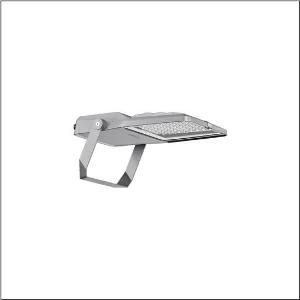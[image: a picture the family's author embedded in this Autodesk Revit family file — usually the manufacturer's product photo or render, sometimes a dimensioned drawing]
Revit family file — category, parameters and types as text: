
# Revit family: floodlight_fl_21_iq_mini___pl64_5xa7772b5e1a_cdb2
name_source: partatom
category: Lighting Fixtures
units: mm (PartAtom-declared; Revit-internal decimal feet)

## family parameters
Cut with Voids When Loaded = No
Host = Face
Light Source = No
Part Type = Normal
Room Calculation Point = No
Round Connector Dimension = Use Diameter
Shared = No

## types (1)
- --- (1 x LED, 5620 lm, 45.5 W, 4000K)
    Apparent Load = 46 VA
    CIE Flux Codes = 28 80 98 100 100
    Color Rendering = 80
    Color Temperature = 4000K
    Default Elevation = 1800 mm
    Description = Floodlight FL 21 iQ mini, floodlight, primary light control with lens, of PMMA, primary optical cover: protective disc, of toughened safety glass, transparent, light distribution: PL64, light emission: direct distribution, installation type: surface-mounted, LED, High Power LED, rated luminous flux: 5.620lm, luminous efficacy: 124lm/W, light colour: 840, colour temperature: 4000K, control: Street-Remote, Auto-Match, Temp-Guard, Night-Set, Smart-Wire, Desk-Remote (wireless, voltage-free reading and setting of iQ features in the workshop via application-optimized NFC function/RFID function), optimised constant luminous flux control (CLO 2.0), with terminal, 6-pole, mains connection: 220..240V, AC, 50/60Hz, start of lifetime: 46W, end of service life: 48W, reduction: 22W, luminaire housing, of diecast aluminium, powder-coated, Siteco® metallic grey (DB 702S), corrosivity category C5 mid according to DIN EN ISO 12944, sealing non-destructively replaceable, mounting bracket, of steel, galvanised, powder-coated, Siteco® metallic grey (DB 702S), protection rating (complete): IP66, insulation class (complete): insulation class II (safety insulation), certification: CE, ENEC, VDE, protection symbol: D, impact resistance: IK08, permissible operating ambient temperature: -40..+40°C, permissible operating ambient temperature for outdoor applications: -40..+50°C, standard: DIN EN 12944, LABS conformity tested according to VDMA 24364:2018-05, packaging unit: 1 piece

Light Distribution: PL64
    Height = 70 mm
    Lamp = 1 x LED
    Lamp Light Flux = 5620 lm
    Lamp Power = 45.5 W
    Lamp count = 1
    Length = 485 mm
    Luminous efficacy = 124 lm/W
    Manufacturer = Siteco
    ModVariant = No
    Model = 5XA7772B5E1A
    Number of Poles = 1
    OnlyDefault = Yes
    Power Factor = 1
    Product Name = Floodlight FL 21 iQ mini | PL64
    Product group = floodlight | pylon annexe
    ProductGroupID = 6200
    Protection Class = Protection class II
    Protection Degree = IP 66
    RLX_Detail_Level = 1
    RLX_Emergency_Light_Flux = 0 lm
    RLX_Emergency_Type = 0
    RLX_Emergency_Type_DB = No
    RlxData = <blob elided: 96197 chars, md5=6bed9cd0>
    Socket = socket
    Standby Power = 0 W
    System Light Flux = 5620 lm
    System Power = 46 W
    Type Comments = factory setting: luminous flux: 100 % | dim-lin: 254 | 463 mA
    Type Image = l_1006845.jpg
    URL = http://relux.com
    VarID = @adj_099021
    Voltage = 0 V
    Weight = 0.00 kg
    Width = 337 mm

## geometry (parser evidence)
native form markers: Blend x4, Sweep x12
no freeform markers — native parametric forms only
